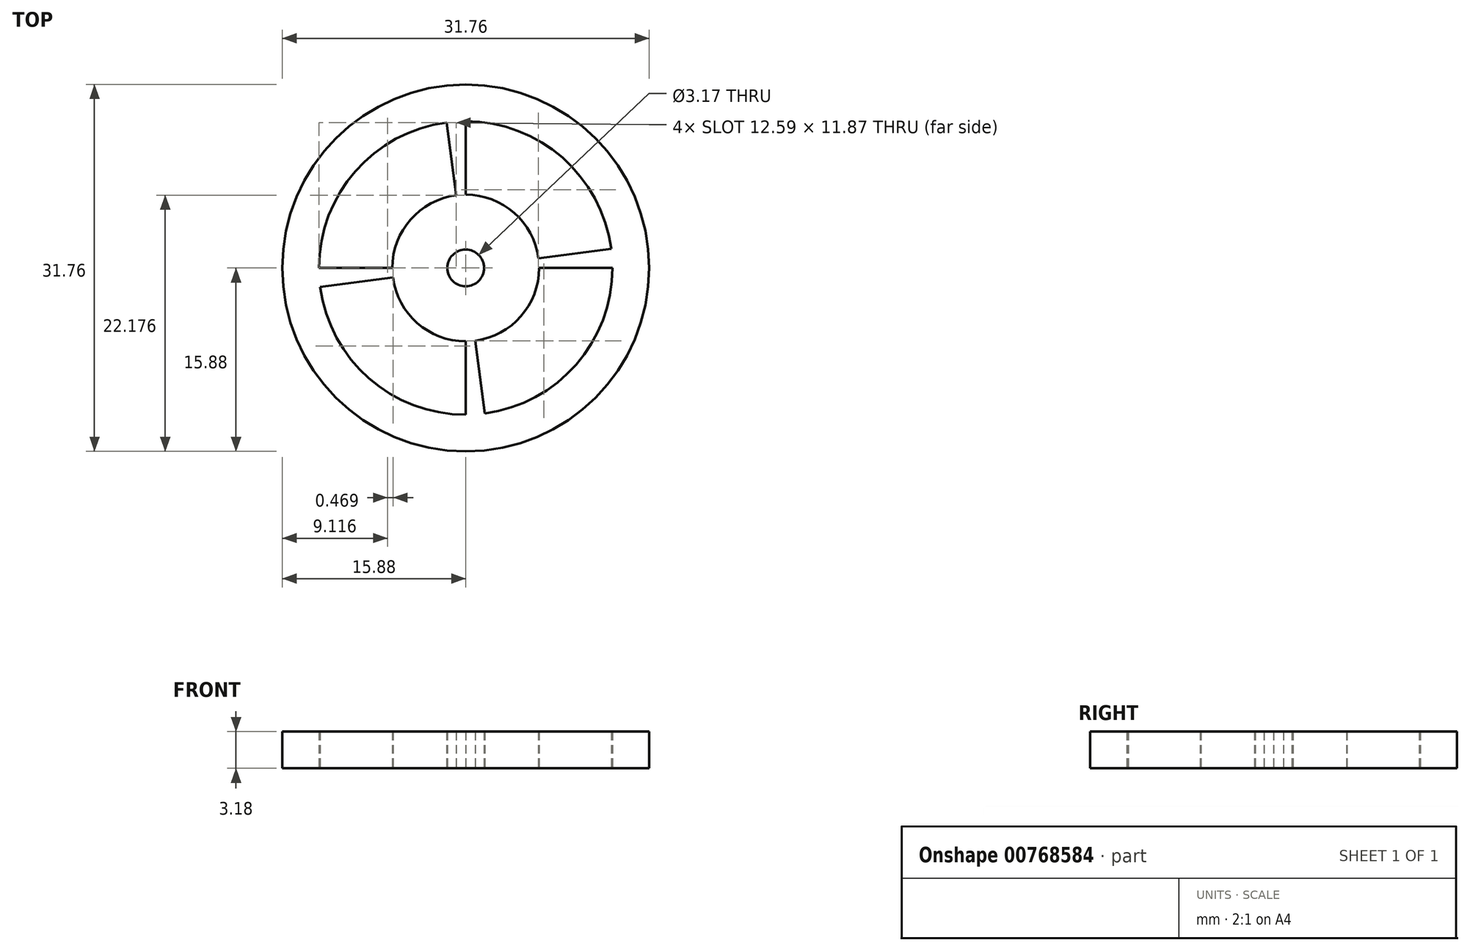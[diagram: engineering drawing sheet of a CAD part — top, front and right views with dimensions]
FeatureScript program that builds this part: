
annotation { "Feature Type Name" : "Feature", "Feature Type Description" : "" }
export const myFeature = defineFeature(function(context is Context, id is Id, definition is map)
    precondition{}
    {
        {
            var Q0;
            Q0=qCreatedBy(makeId("Top.planeOp"),FACE);
            var sketch = newSketch(context, id + "F0", { "sketchPlane" : qUnion([Q0])});
            skCircle(sketch, "E0", {"center": v(0, 0) * mm, "radius": 15.88 * mm});
            skCircle(sketch, "E1", {"center": v(0, 0) * mm, "radius": 1.59 * mm});
            skCircle(sketch, "E2", {"center": v(0, 0) * mm, "radius": 6.35 * mm});
            skCircle(sketch, "E3", {"center": v(0, 0) * mm, "radius": 12.7 * mm});
            skLineSegment(sketch, "E4", {"start": v(0, 0) * mm, "end": v(-2.07, 15.74) * mm});
            skLineSegment(sketch, "E5", {"start": v(0, 0) * mm, "end": v(0, 15.88) * mm});
            skLineSegment(sketch, "E6", {"start": v(0, 0) * mm, "end": v(15.88, 0) * mm});
            skLineSegment(sketch, "E7", {"start": v(0, 0) * mm, "end": v(0, -15.88) * mm});
            skLineSegment(sketch, "E8", {"start": v(0, 0) * mm, "end": v(15.74, 2.07) * mm});
            skLineSegment(sketch, "E9", {"start": v(0, 0) * mm, "end": v(2.07, -15.74) * mm});
            skLineSegment(sketch, "E10", {"start": v(0, 0) * mm, "end": v(-15.74, -2.07) * mm});
            skLineSegment(sketch, "E11", {"start": v(0, 0) * mm, "end": v(-15.88, 0) * mm});
            skSolve(sketch);
        }
        {
            var Q0;
            {var subQ0=sQuery(id+"F0.wireOp",EDGE,"E11");var subQ1=sQuery(id+"F0.wireOp",EDGE,"E1");var subQ2=makeQuery(id+"F0.imprint","INTERSECT",VERTEX,{"derivedFrom":[subQ1,subQ0]});Q0=makeQuery(id+"F0.imprint","IMPRINT",FACE,{"disambiguationData":[TD([[makeQuery(id+"F0.imprint","IMPRINT",EDGE,{"disambiguationData":[TD([[subQ2,-1.0]])],"derivedFrom":subQ1}),-1.0]])]});}
            var Q1;
            {var subQ0=sQuery(id+"F0.wireOp",EDGE,"E10");var subQ1=sQuery(id+"F0.wireOp",EDGE,"E0");var subQ2=makeQuery(id+"F0.imprint","INTERSECT",VERTEX,{"derivedFrom":[subQ1,subQ0]});Q1=makeQuery(id+"F0.imprint","IMPRINT",FACE,{"disambiguationData":[TD([[makeQuery(id+"F0.imprint","IMPRINT",EDGE,{"disambiguationData":[TD([[subQ2,1.0]])],"derivedFrom":subQ1}),1.0]])]});}
            var Q2;
            {var subQ0=sQuery(id+"F0.wireOp",EDGE,"E7");var subQ1=sQuery(id+"F0.wireOp",EDGE,"E1");var subQ2=makeQuery(id+"F0.imprint","INTERSECT",VERTEX,{"derivedFrom":[subQ1,subQ0]});Q2=makeQuery(id+"F0.imprint","IMPRINT",FACE,{"disambiguationData":[TD([[makeQuery(id+"F0.imprint","IMPRINT",EDGE,{"disambiguationData":[TD([[subQ2,-1.0]])],"derivedFrom":subQ1}),-1.0]])]});}
            var Q3;
            {var subQ0=sQuery(id+"F0.wireOp",EDGE,"E5");var subQ1=sQuery(id+"F0.wireOp",EDGE,"E1");var subQ2=makeQuery(id+"F0.imprint","INTERSECT",VERTEX,{"derivedFrom":[subQ1,subQ0]});Q3=makeQuery(id+"F0.imprint","IMPRINT",FACE,{"disambiguationData":[TD([[makeQuery(id+"F0.imprint","IMPRINT",EDGE,{"disambiguationData":[TD([[subQ2,-1.0]])],"derivedFrom":subQ1}),-1.0]])]});}
            var Q4;
            {var subQ0=sQuery(id+"F0.wireOp",EDGE,"E8");var subQ1=sQuery(id+"F0.wireOp",EDGE,"E1");var subQ2=makeQuery(id+"F0.imprint","INTERSECT",VERTEX,{"derivedFrom":[subQ1,subQ0]});Q4=makeQuery(id+"F0.imprint","IMPRINT",FACE,{"disambiguationData":[TD([[makeQuery(id+"F0.imprint","IMPRINT",EDGE,{"disambiguationData":[TD([[subQ2,1.0]])],"derivedFrom":subQ1}),-1.0]])]});}
            var Q5;
            {var subQ0=sQuery(id+"F0.wireOp",EDGE,"E7");var subQ1=sQuery(id+"F0.wireOp",EDGE,"E0");var subQ2=makeQuery(id+"F0.imprint","INTERSECT",VERTEX,{"derivedFrom":[subQ1,subQ0]});Q5=makeQuery(id+"F0.imprint","IMPRINT",FACE,{"disambiguationData":[TD([[makeQuery(id+"F0.imprint","IMPRINT",EDGE,{"disambiguationData":[TD([[subQ2,1.0]])],"derivedFrom":subQ1}),1.0]])]});}
            var Q6;
            {var subQ0=sQuery(id+"F0.wireOp",EDGE,"E4");var subQ1=sQuery(id+"F0.wireOp",EDGE,"E0");var subQ2=makeQuery(id+"F0.imprint","INTERSECT",VERTEX,{"derivedFrom":[subQ1,subQ0]});Q6=makeQuery(id+"F0.imprint","IMPRINT",FACE,{"disambiguationData":[TD([[makeQuery(id+"F0.imprint","IMPRINT",EDGE,{"disambiguationData":[TD([[subQ2,-1.0]])],"derivedFrom":subQ1}),1.0]])]});}
            var Q7;
            {var subQ0=sQuery(id+"F0.wireOp",EDGE,"E5");var subQ1=sQuery(id+"F0.wireOp",EDGE,"E0");var subQ2=makeQuery(id+"F0.imprint","INTERSECT",VERTEX,{"derivedFrom":[subQ1,subQ0]});Q7=makeQuery(id+"F0.imprint","IMPRINT",FACE,{"disambiguationData":[TD([[makeQuery(id+"F0.imprint","IMPRINT",EDGE,{"disambiguationData":[TD([[subQ2,1.0]])],"derivedFrom":subQ1}),1.0]])]});}
            var Q8;
            {var subQ0=sQuery(id+"F0.wireOp",EDGE,"E6");var subQ1=sQuery(id+"F0.wireOp",EDGE,"E0");var subQ2=makeQuery(id+"F0.imprint","INTERSECT",VERTEX,{"derivedFrom":[subQ1,subQ0]});Q8=makeQuery(id+"F0.imprint","IMPRINT",FACE,{"disambiguationData":[TD([[makeQuery(id+"F0.imprint","IMPRINT",EDGE,{"disambiguationData":[TD([[subQ2,1.0]])],"derivedFrom":subQ1}),1.0]])]});}
            var Q9;
            {var subQ0=sQuery(id+"F0.wireOp",EDGE,"E7");var subQ1=sQuery(id+"F0.wireOp",EDGE,"E0");var subQ2=makeQuery(id+"F0.imprint","INTERSECT",VERTEX,{"derivedFrom":[subQ1,subQ0]});Q9=makeQuery(id+"F0.imprint","IMPRINT",FACE,{"disambiguationData":[TD([[makeQuery(id+"F0.imprint","IMPRINT",EDGE,{"disambiguationData":[TD([[subQ2,-1.0]])],"derivedFrom":subQ1}),1.0]])]});}
            var Q10;
            {var subQ0=sQuery(id+"F0.wireOp",EDGE,"E6");var subQ1=sQuery(id+"F0.wireOp",EDGE,"E0");var subQ2=makeQuery(id+"F0.imprint","INTERSECT",VERTEX,{"derivedFrom":[subQ1,subQ0]});Q10=makeQuery(id+"F0.imprint","IMPRINT",FACE,{"disambiguationData":[TD([[makeQuery(id+"F0.imprint","IMPRINT",EDGE,{"disambiguationData":[TD([[subQ2,-1.0]])],"derivedFrom":subQ1}),1.0]])]});}
            var Q11;
            {var subQ0=sQuery(id+"F0.wireOp",EDGE,"E4");var subQ1=sQuery(id+"F0.wireOp",EDGE,"E0");var subQ2=makeQuery(id+"F0.imprint","INTERSECT",VERTEX,{"derivedFrom":[subQ1,subQ0]});Q11=makeQuery(id+"F0.imprint","IMPRINT",FACE,{"disambiguationData":[TD([[makeQuery(id+"F0.imprint","IMPRINT",EDGE,{"disambiguationData":[TD([[subQ2,1.0]])],"derivedFrom":subQ1}),1.0]])]});}
            var Q12;
            {var subQ0=sQuery(id+"F0.wireOp",EDGE,"E11");var subQ1=sQuery(id+"F0.wireOp",EDGE,"E2");var subQ2=makeQuery(id+"F0.imprint","INTERSECT",VERTEX,{"derivedFrom":[subQ1,subQ0]});Q12=makeQuery(id+"F0.imprint","IMPRINT",FACE,{"disambiguationData":[TD([[makeQuery(id+"F0.imprint","IMPRINT",EDGE,{"disambiguationData":[TD([[subQ2,-1.0]])],"derivedFrom":subQ1}),-1.0]])]});}
            var Q13;
            {var subQ0=sQuery(id+"F0.wireOp",EDGE,"E10");var subQ1=sQuery(id+"F0.wireOp",EDGE,"E1");var subQ2=makeQuery(id+"F0.imprint","INTERSECT",VERTEX,{"derivedFrom":[subQ1,subQ0]});Q13=makeQuery(id+"F0.imprint","IMPRINT",FACE,{"disambiguationData":[TD([[makeQuery(id+"F0.imprint","IMPRINT",EDGE,{"disambiguationData":[TD([[subQ2,-1.0]])],"derivedFrom":subQ1}),-1.0]])]});}
            var Q14;
            {var subQ0=sQuery(id+"F0.wireOp",EDGE,"E6");var subQ1=sQuery(id+"F0.wireOp",EDGE,"E1");var subQ2=makeQuery(id+"F0.imprint","INTERSECT",VERTEX,{"derivedFrom":[subQ1,subQ0]});Q14=makeQuery(id+"F0.imprint","IMPRINT",FACE,{"disambiguationData":[TD([[makeQuery(id+"F0.imprint","IMPRINT",EDGE,{"disambiguationData":[TD([[subQ2,1.0]])],"derivedFrom":subQ1}),-1.0]])]});}
            var Q15;
            {var subQ0=sQuery(id+"F0.wireOp",EDGE,"E8");var subQ1=sQuery(id+"F0.wireOp",EDGE,"E1");var subQ2=makeQuery(id+"F0.imprint","INTERSECT",VERTEX,{"derivedFrom":[subQ1,subQ0]});Q15=makeQuery(id+"F0.imprint","IMPRINT",FACE,{"disambiguationData":[TD([[makeQuery(id+"F0.imprint","IMPRINT",EDGE,{"disambiguationData":[TD([[subQ2,-1.0]])],"derivedFrom":subQ1}),-1.0]])]});}
            var Q16;
            {var subQ0=sQuery(id+"F0.wireOp",EDGE,"E4");var subQ1=sQuery(id+"F0.wireOp",EDGE,"E1");var subQ2=makeQuery(id+"F0.imprint","INTERSECT",VERTEX,{"derivedFrom":[subQ1,subQ0]});Q16=makeQuery(id+"F0.imprint","IMPRINT",FACE,{"disambiguationData":[TD([[makeQuery(id+"F0.imprint","IMPRINT",EDGE,{"disambiguationData":[TD([[subQ2,-1.0]])],"derivedFrom":subQ1}),-1.0]])]});}
            var Q17;
            {var subQ0=sQuery(id+"F0.wireOp",EDGE,"E5");var subQ1=sQuery(id+"F0.wireOp",EDGE,"E2");var subQ2=makeQuery(id+"F0.imprint","INTERSECT",VERTEX,{"derivedFrom":[subQ1,subQ0]});Q17=makeQuery(id+"F0.imprint","IMPRINT",FACE,{"disambiguationData":[TD([[makeQuery(id+"F0.imprint","IMPRINT",EDGE,{"disambiguationData":[TD([[subQ2,-1.0]])],"derivedFrom":subQ1}),-1.0]])]});}
            var Q18;
            {var subQ0=sQuery(id+"F0.wireOp",EDGE,"E8");var subQ1=sQuery(id+"F0.wireOp",EDGE,"E2");var subQ2=makeQuery(id+"F0.imprint","INTERSECT",VERTEX,{"derivedFrom":[subQ1,subQ0]});Q18=makeQuery(id+"F0.imprint","IMPRINT",FACE,{"disambiguationData":[TD([[makeQuery(id+"F0.imprint","IMPRINT",EDGE,{"disambiguationData":[TD([[subQ2,1.0]])],"derivedFrom":subQ1}),-1.0]])]});}
            var Q19;
            {var subQ0=sQuery(id+"F0.wireOp",EDGE,"E7");var subQ1=sQuery(id+"F0.wireOp",EDGE,"E2");var subQ2=makeQuery(id+"F0.imprint","INTERSECT",VERTEX,{"derivedFrom":[subQ1,subQ0]});Q19=makeQuery(id+"F0.imprint","IMPRINT",FACE,{"disambiguationData":[TD([[makeQuery(id+"F0.imprint","IMPRINT",EDGE,{"disambiguationData":[TD([[subQ2,-1.0]])],"derivedFrom":subQ1}),-1.0]])]});}
            extrude(context, id + "F1", {"entities" : qUnion([Q0, Q1, Q2, Q3, Q4, Q5, Q6, Q7, Q8, Q9, Q10, Q11, Q12, Q13, Q14, Q15, Q16, Q17, Q18, Q19]), "depth" : 3.17 * mm, "offsetDistance" : 25.4 * mm});
        }
    });
